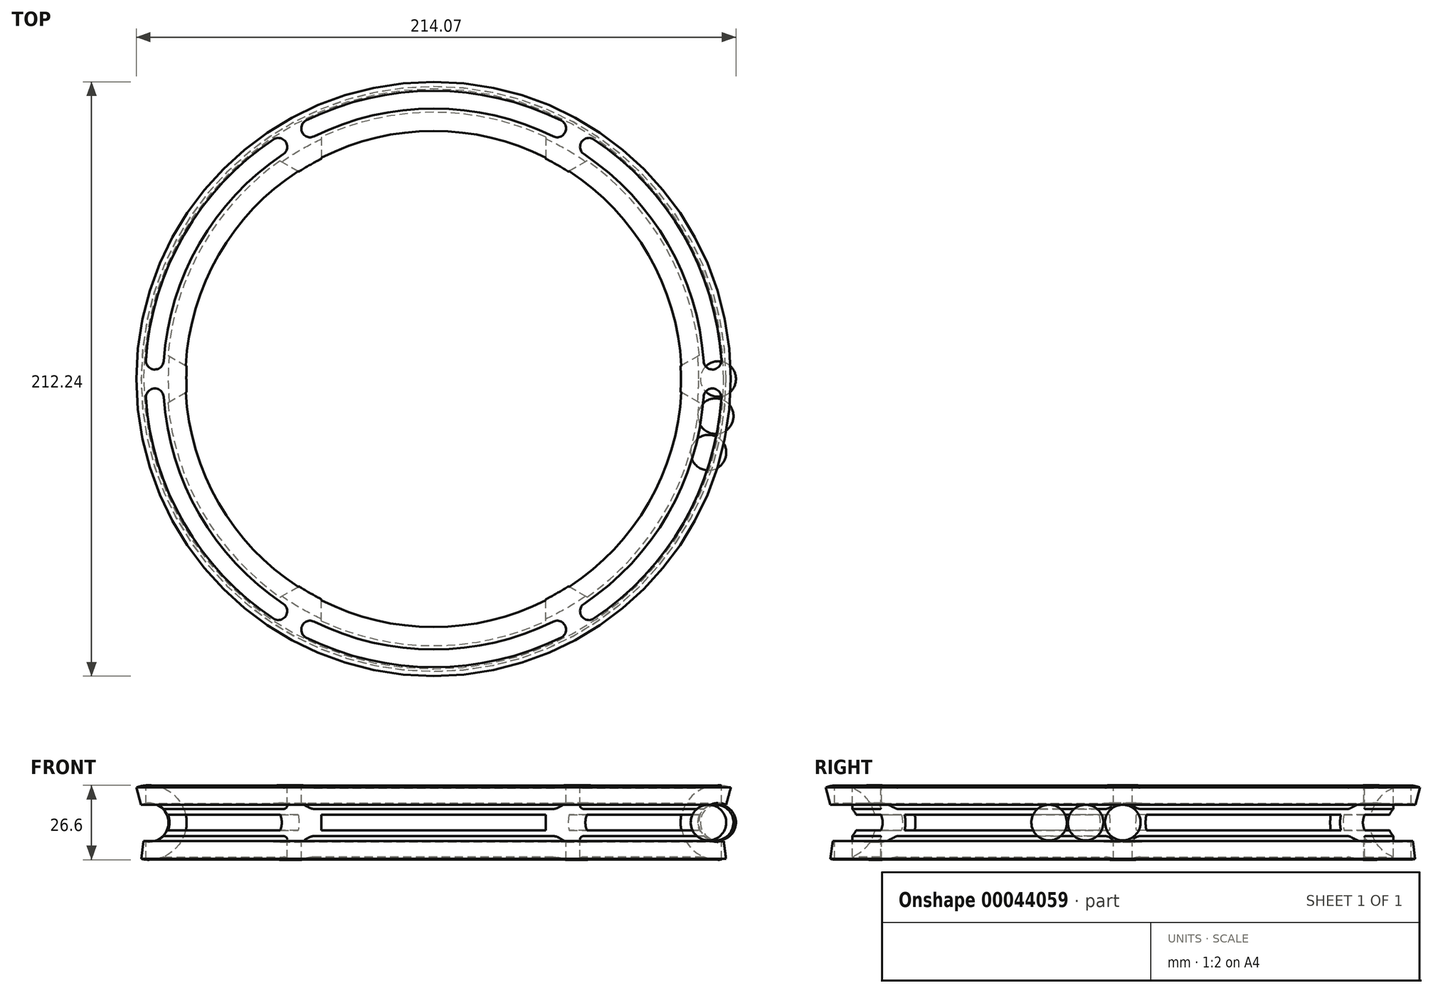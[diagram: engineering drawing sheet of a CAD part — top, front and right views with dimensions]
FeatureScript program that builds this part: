
annotation { "Feature Type Name" : "Feature", "Feature Type Description" : "" }
export const myFeature = defineFeature(function(context is Context, id is Id, definition is map)
    precondition{}
    {
        {
            var Q0;
            Q0=qCreatedBy(makeId("Front.planeOp"),FACE);
            var sketch = newSketch(context, id + "F0", { "sketchPlane" : qUnion([Q0])});
            skArc(sketch, "E0", {"start": v(104.45, 6.34) * mm, "mid": v(94.66, 0.46) * mm, "end": v(103.6, -6.66) * mm});
            skArc(sketch, "E1.0", {"start": v(106.12, 12.5) * mm, "mid": v(88.33, 0.9) * mm, "end": v(104.4, -13) * mm});
            skLineSegment(sketch, "E2", {"start": v(104.45, 6.34) * mm, "end": v(106.12, 12.5) * mm});
            skLineSegment(sketch, "E3", {"start": v(104.4, -13) * mm, "end": v(103.6, -6.66) * mm});
            skLineSegment(sketch, "E4", {"start": v(0, 22.2) * mm, "end": v(0, -13.55) * mm, "construction": true});
            skSolve(sketch);
        }
        {
            var Q0;
            Q0 = qSketchRegion(id + "F0", true);
            var Q1;
            Q1=sQuery(id+"F0.wireOp",EDGE,"E4");
            revolve(context, id + "F1", {"entities" : qUnion([Q0]), "axis" : qUnion([Q1]), "revolveType" : RevolveType.FULL});
        }
        {
            var Q0;
            Q0=qCreatedBy(makeId("Right.planeOp"),FACE);
            var sketch = newSketch(context, id + "F2", { "sketchPlane" : qUnion([Q0])});
            skLineSegment(sketch, "E5", {"start": v(0, 23.82) * mm, "end": v(0, -28.67) * mm, "construction": true});
            skSolve(sketch);
        }
        {
            var Q0;
            Q0=qCreatedBy(makeId("Top.planeOp"),FACE);
            var sketch = newSketch(context, id + "F3", { "sketchPlane" : qUnion([Q0])});
            skArc(sketch, "E6.0", {"start": v(45.5, 92.35) * mm, "mid": v(0, 102.95) * mm, "end": v(-45.5, 92.35) * mm});
            skPoint(sketch, "E7", {"position": v(0, 102.95) * mm});
            skPoint(sketch, "E8", {"position": v(45.5, 92.35) * mm});
            skPoint(sketch, "E9", {"position": v(-45.5, 92.35) * mm});
            skArc(sketch, "E10.0", {"start": v(42.69, 86.66) * mm, "mid": v(0, 96.6) * mm, "end": v(-42.69, 86.66) * mm});
            skArc(sketch, "E11", {"start": v(-42.69, 86.66) * mm, "mid": v(-46.94, 88.1) * mm, "end": v(-45.5, 92.35) * mm});
            skArc(sketch, "E12", {"start": v(42.69, 86.66) * mm, "mid": v(46.94, 88.1) * mm, "end": v(45.5, 92.35) * mm});
            skSolve(sketch);
        }
        {
            var Q0;
            Q0 = qSketchRegion(id + "F3", true);
            extrude(context, id + "F4", {"entities" : qUnion([Q0]), "operationType" : NewBodyOperationType.REMOVE, "endBound" : BoundingType.THROUGH_ALL, "oppositeDirection" : true, "depth" : 25.4 * mm, "hasSecondDirection" : true, "secondDirectionBound" : BoundingType.THROUGH_ALL, "secondDirectionOppositeDirection" : false, "secondDirectionDepth" : 25.4 * mm});
        }
        {
            var Q0;
            Q0=makeQuery(id+"F1.opRevolve","SWEPT_BODY",BODY,{"disambiguationData":[OSD([sQuery(id+"F0.wireOp",EDGE,"E0"),sQuery(id+"F0.wireOp",EDGE,"E1.0"),sQuery(id+"F0.wireOp",EDGE,"E2"),sQuery(id+"F0.wireOp",EDGE,"E3")])]});
            var Q1;
            Q1=makeQuery(id+"F4.boolean.opBoolean","COPY",FACE,{"disambiguationData":[OD(1.0)],"derivedFrom":makeQuery(id+"F4.opExtrude","SWEPT_FACE",FACE,{"disambiguationData":[OSD([sQuery(id+"F3.wireOp",EDGE,"E10.0")])]})});
            var Q2;
            Q2=makeQuery(id+"F4.boolean.opBoolean","COPY",FACE,{"disambiguationData":[OD(1.0)],"derivedFrom":makeQuery(id+"F4.opExtrude","SWEPT_FACE",FACE,{"disambiguationData":[OSD([sQuery(id+"F3.wireOp",EDGE,"E11")])]})});
            var Q3;
            Q3=makeQuery(id+"F4.boolean.opBoolean","COPY",FACE,{"disambiguationData":[OD(1.0)],"derivedFrom":makeQuery(id+"F4.opExtrude","SWEPT_FACE",FACE,{"disambiguationData":[OSD([sQuery(id+"F3.wireOp",EDGE,"E6.0")])]})});
            var Q4;
            Q4=makeQuery(id+"F4.boolean.opBoolean","COPY",FACE,{"disambiguationData":[OD(1.0)],"derivedFrom":makeQuery(id+"F4.opExtrude","SWEPT_FACE",FACE,{"disambiguationData":[OSD([sQuery(id+"F3.wireOp",EDGE,"E12")])]})});
            var Q5;
            Q5=makeQuery(id+"F4.boolean.opBoolean","COPY",FACE,{"disambiguationData":[OD(0.0)],"derivedFrom":makeQuery(id+"F4.opExtrude","SWEPT_FACE",FACE,{"disambiguationData":[OSD([sQuery(id+"F3.wireOp",EDGE,"E10.0")])]})});
            var Q6;
            Q6=makeQuery(id+"F4.boolean.opBoolean","COPY",FACE,{"disambiguationData":[OD(0.0)],"derivedFrom":makeQuery(id+"F4.opExtrude","SWEPT_FACE",FACE,{"disambiguationData":[OSD([sQuery(id+"F3.wireOp",EDGE,"E6.0")])]})});
            var Q7;
            Q7=makeQuery(id+"F4.boolean.opBoolean","COPY",FACE,{"disambiguationData":[OD(0.0)],"derivedFrom":makeQuery(id+"F4.opExtrude","SWEPT_FACE",FACE,{"disambiguationData":[OSD([sQuery(id+"F3.wireOp",EDGE,"E12")])]})});
            var Q8;
            Q8=makeQuery(id+"F4.boolean.opBoolean","COPY",FACE,{"disambiguationData":[OD(0.0)],"derivedFrom":makeQuery(id+"F4.opExtrude","SWEPT_FACE",FACE,{"disambiguationData":[OSD([sQuery(id+"F3.wireOp",EDGE,"E11")])]})});
            var Q9;
            Q9=sQuery(id+"F2.wireOp",EDGE,"E5");
            circularPattern(context, id + "F5", {"faces" : qUnion([Q1, Q2, Q3, Q4, Q5, Q6, Q7, Q8]), "axis" : qUnion([Q9]), "angle" : 360 * degree, "instanceCount" : 6, "equalSpace" : true, "patternType" : PatternType.FACE, "computeTransformsWithoutBuiltin" : true});
        }
        {
            var Q0;
            Q0=qCreatedBy(makeId("Front.planeOp"),FACE);
            var sketch = newSketch(context, id + "F6", { "sketchPlane" : qUnion([Q0])});
            skLineSegment(sketch, "E13", {"start": v(101.6, -6.35) * mm, "end": v(101.6, 6.35) * mm});
            skArc(sketch, "E14", {"start": v(101.6, -6.35) * mm, "mid": v(107.95, 0) * mm, "end": v(101.6, 6.35) * mm});
            skLineSegment(sketch, "E15", {"start": v(101.6, 0) * mm, "end": v(101.6, 17.07) * mm});
            skLineSegment(sketch, "E16", {"start": v(101.6, 17.07) * mm, "end": v(101.6, -14.7) * mm});
            skSolve(sketch);
        }
        {
            var Q0;
            {var subQ1=sQuery(id+"F6.wireOp",EDGE,"E14");Q0=makeQuery(id+"F6.imprint","IMPRINT",FACE,{"disambiguationData":[TD([[makeQuery(id+"F6.imprint","IMPRINT",EDGE,{"derivedFrom":subQ1}),1.0]])]});}
            var Q1;
            Q1=sQuery(id+"F6.wireOp",EDGE,"E16");
            revolve(context, id + "F7", {"entities" : qUnion([Q0]), "axis" : qUnion([Q1]), "revolveType" : RevolveType.FULL});
        }
        {
            var Q0;
            Q0=qCreatedBy(makeId("Front.planeOp"),FACE);
            var sketch = newSketch(context, id + "F8", { "sketchPlane" : qUnion([Q0])});
            skLineSegment(sketch, "E17.rect.bottom", {"start": v(40.1, -2.83) * mm, "end": v(-40.1, -2.83) * mm});
            skLineSegment(sketch, "E17.rect.top", {"start": v(40.1, 2.83) * mm, "end": v(-40.1, 2.83) * mm});
            skLineSegment(sketch, "E17.rect.left", {"start": v(40.1, -2.83) * mm, "end": v(40.1, 2.83) * mm});
            skLineSegment(sketch, "E17.rect.right", {"start": v(-40.1, -2.83) * mm, "end": v(-40.1, 2.83) * mm});
            skPoint(sketch, "E17.rect.middle", {"position": v(0, 0) * mm});
            skSolve(sketch);
        }
        {
            var Q0;
            Q0 = qSketchRegion(id + "F8", true);
            extrude(context, id + "F9", {"entities" : qUnion([Q0]), "operationType" : NewBodyOperationType.REMOVE, "endBound" : BoundingType.THROUGH_ALL, "oppositeDirection" : true, "depth" : 25.4 * mm});
        }
        {
            var Q0;
            Q0=makeQuery(id+"F9.boolean.opBoolean","COPY",FACE,{"derivedFrom":makeQuery(id+"F9.opExtrude","SWEPT_FACE",FACE,{"disambiguationData":[OSD([sQuery(id+"F8.wireOp",EDGE,"E17.rect.bottom")])]})});
            var Q1;
            Q1=makeQuery(id+"F9.boolean.opBoolean","COPY",FACE,{"derivedFrom":makeQuery(id+"F9.opExtrude","SWEPT_FACE",FACE,{"disambiguationData":[OSD([sQuery(id+"F8.wireOp",EDGE,"E17.rect.top")])]})});
            var Q2;
            Q2=makeQuery(id+"F9.boolean.opBoolean","COPY",FACE,{"derivedFrom":makeQuery(id+"F9.opExtrude","SWEPT_FACE",FACE,{"disambiguationData":[OSD([sQuery(id+"F8.wireOp",EDGE,"E17.rect.right")])]})});
            var Q3;
            Q3=makeQuery(id+"F9.boolean.opBoolean","COPY",FACE,{"derivedFrom":makeQuery(id+"F9.opExtrude","SWEPT_FACE",FACE,{"disambiguationData":[OSD([sQuery(id+"F8.wireOp",EDGE,"E17.rect.left")])]})});
            var Q4;
            Q4=sQuery(id+"F2.wireOp",EDGE,"E5");
            circularPattern(context, id + "F10", {"operationType" : NewBodyOperationType.ADD, "faces" : qUnion([Q0, Q1, Q2, Q3]), "axis" : qUnion([Q4]), "angle" : 360 * degree, "instanceCount" : 6, "oppositeDirection" : true, "equalSpace" : true, "patternType" : PatternType.FACE, "computeTransformsWithoutBuiltin" : true});
        }
        {
            var Q0;
            Q0=makeQuery(id+"F7.opRevolve","SWEPT_BODY",BODY,{"disambiguationData":[OSD([sQuery(id+"F6.wireOp",EDGE,"E14"),sQuery(id+"F6.wireOp",EDGE,"E16")])]});
            var Q1;
            Q1=sQuery(id+"F0.wireOp",EDGE,"E4");
            circularPattern(context, id + "F11", {"entities" : qUnion([Q0]), "axis" : qUnion([Q1]), "angle" : 15 * degree, "instanceCount" : 3, "equalSpace" : true, "computeTransformsWithoutBuiltin" : true});
        }
    });
